# Revit family: LED-TR
name_source: partatom
category: Lighting Fixtures
revit_build: Autodesk Revit 2014 (Build: 20130308_1515(x64)
units: mm (PartAtom-declared; Revit-internal decimal feet)

## types (2) — shared parameters
Apparent Load = 52 VA
Assembly Code = D5020200
Color Filter = 16777215
Connector Description = Lighting Connector
Default Elevation = 48"
Description = LED Troffer with Advanced Solid State Technology. Long-life 50,000 hour LEDs at L70 lumen maintenance reduce facility maintenance needs.
Dimming Lamp Color Temperature Shift = <None>
Drum-Height = 24"
Emit Shape Visible in Rendering = No
Emit from Rectangle Length = 24"
Features = Full distribution LED troffer
• Direct replacement for fluorescent
• Long-life, 50,000 hour LEDs at L70 reduce life cycle maintenance costs
• Three LED color choices
• Many shielding choices
• Two door frame choices
• Recessed, surface, or cable mount
• Metal to metal light leak protection on all four sides of shielding frame
• Fixed output, step dimming (high/low/off), or 0-10V dimming drivers
• Hinged optical system allows easy access to LED modules and electrical
 from below the ceiling
• Field serviceable components
Fixture distribution = Direct
Housing Material = Paint - Hubbell - Matte White
Lamp = LED
Load Classification = Lighting
Manufacturer = Whiteway
Model = LED-TR Linear Facade
Photometric Web File = generic.ies
Power Factor = 1
Product Documentation Link = https://hubbellcdn.com
Product Link = https://www.hubbell.com
Reflector Finish = Hubbell - White Glass
Tilt Angle = -90.00°
URL = https://www.hubbell.com
Voltage = 120 V
Warranty = 5 years Warranty
Wattage Comments = 52W
Watts = 52 W
Width = 24"
Wings = Paint - Hubbell - Light Silver

## per-type parameters (varying)
| type | Emit from Rectangle Width | Length |
| LED-TR-22 | 24" | 24" |
| LED-TR-24 | 48" | 48" |

## geometry (parser evidence)
native form markers: Sweep x3
no freeform markers — native parametric forms only
